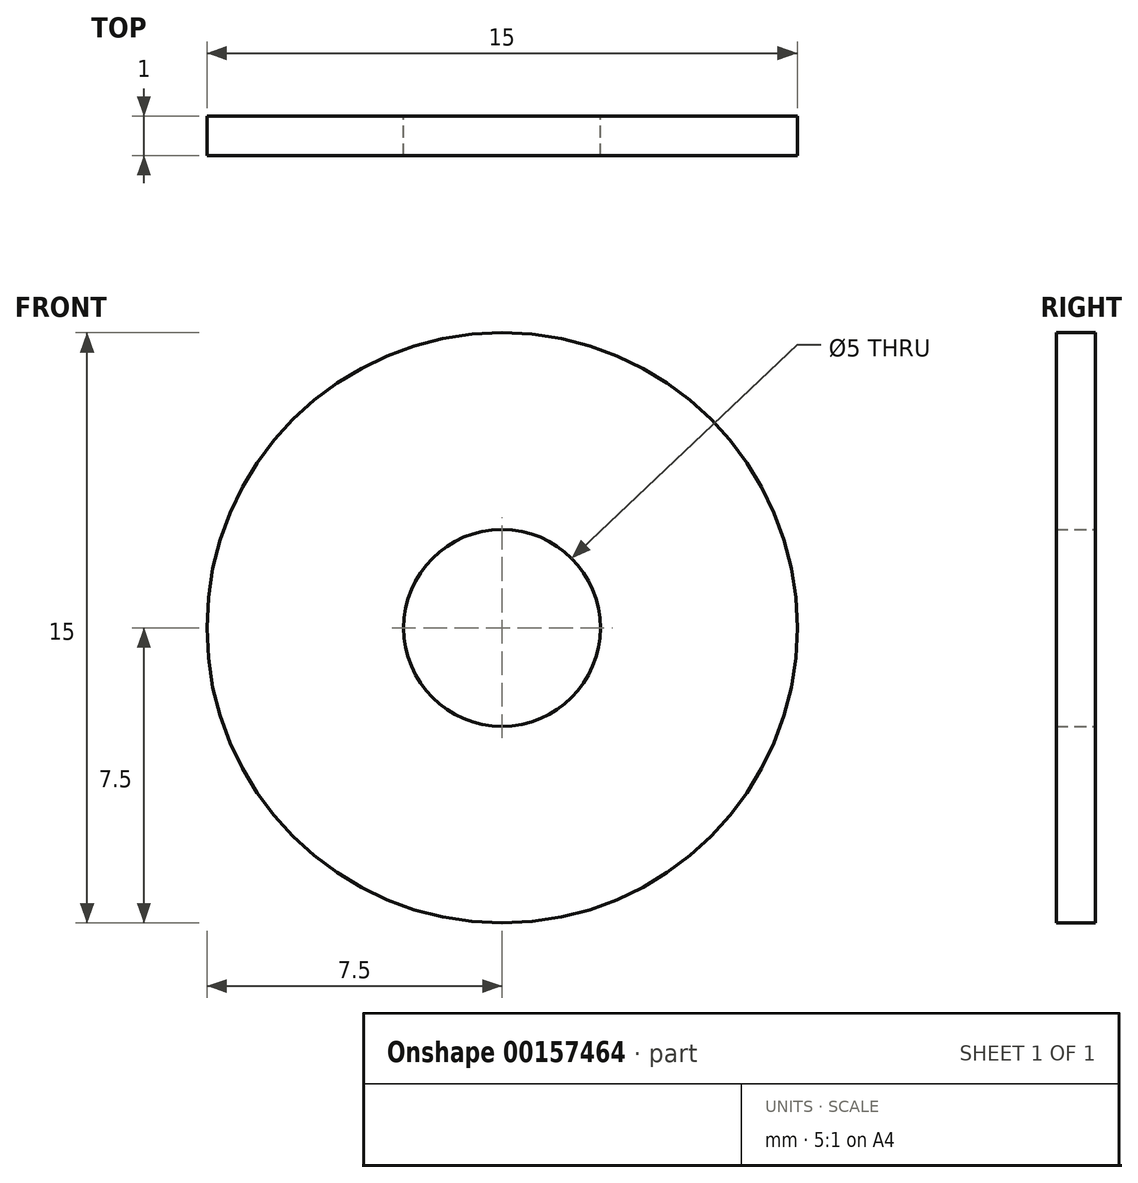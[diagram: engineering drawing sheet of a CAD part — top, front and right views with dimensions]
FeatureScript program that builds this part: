
annotation { "Feature Type Name" : "Feature", "Feature Type Description" : "" }
export const myFeature = defineFeature(function(context is Context, id is Id, definition is map)
    precondition{}
    {
        {
            var Q0;
            Q0=qCreatedBy(makeId("Front.planeOp"),FACE);
            var sketch = newSketch(context, id + "F0", { "sketchPlane" : qUnion([Q0])});
            skCircle(sketch, "E0", {"center": v(0, 0) * mm, "radius": 7.5 * mm});
            skCircle(sketch, "E1", {"center": v(0, 0) * mm, "radius": 2.5 * mm});
            skSolve(sketch);
        }
        {
            var Q0;
            Q0=makeQuery(id+"F0.imprint","IMPRINT",FACE,{"disambiguationData":[TD([[makeQuery(id+"F0.imprint","IMPRINT",EDGE,{"derivedFrom":sQuery(id+"F0.wireOp",EDGE,"E0")}),1.0]])]});
            extrude(context, id + "F1", {"entities" : qUnion([Q0]), "depth" : 1 * mm});
        }
    });
